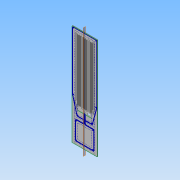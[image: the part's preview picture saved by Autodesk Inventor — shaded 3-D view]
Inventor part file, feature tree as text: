
AUTODESK INVENTOR PART (.ipt)
format: ipt  version: 2013 (Build 170138000, 138)  size: 448,000 bytes
history: native  units: in
note: dims shown in document units (in); Inventor stores cm internally (conversion verified against a paired STEP export)
features: other x15, extrude x5, hole x1, plane x1
ambient origin geometry x8: Origin, YZ Plane, XZ Plane, XY Plane, X Axis, Y Axis, Z Axis, Center Point
bodies: Solid1 (feature_tree)
feature tree (22):
  other  "Blocks"
  extrude  "Stock Extrusion"  Depth=23.8125in
  extrude  "Main rope pocket"  Depth=96.0in
  other  "Side profile reference"
  hole  "Hole1"  [1 undecoded]
  plane  "Work Plane1"
  extrude  "Through Panel Extrusion5"  Depth=58.0in
  other  "Exclaim Point"
  other  "Removal extra wood"
  other  "SignCenter"
  extrude  "Point pocket"  Depth=1.0in
  extrude  "Remove extra wood"  Depth=2.9062in
  other  "Stock"
  other  "LEDPocket"
  other  "TwoLineColumn"
  other  "TwoLineColumnEnd"
  other  "15mm Neon profile"
  other  "U Bolt hole and bore"
  other  "U-Bolt holes"
  other  "WeatherProof panel"
  other  "15mm Neon profile:1"
  other  "15mm Neon profile:2"
note: 1 required parameter value undecoded (feature->parameter linkage not recoverable at this tier; creation-order binding heuristic only, values carry confidence <= 0.55)
